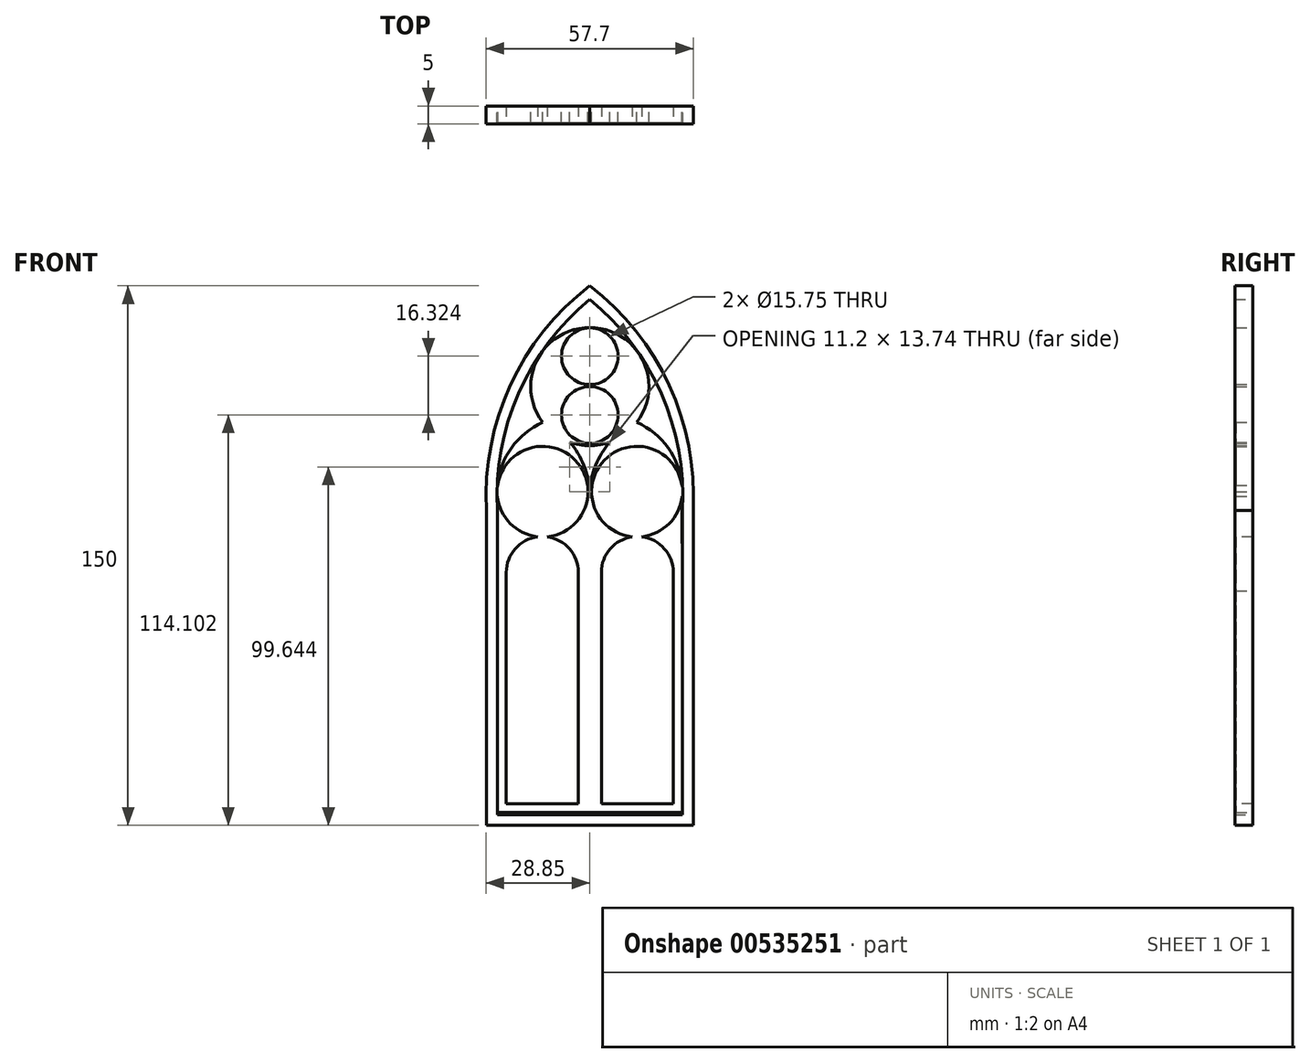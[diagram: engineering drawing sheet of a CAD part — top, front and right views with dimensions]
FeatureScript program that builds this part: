
annotation { "Feature Type Name" : "Feature", "Feature Type Description" : "" }
export const myFeature = defineFeature(function(context is Context, id is Id, definition is map)
    precondition{}
    {
        {
            var Q0;
            Q0=qCreatedBy(makeId("Front.planeOp"),FACE);
            var sketch = newSketch(context, id + "F0", { "sketchPlane" : qUnion([Q0])});
            skLineSegment(sketch, "E0", {"start": v(0, 62.4) * mm, "end": v(0, -107.6) * mm, "construction": true});
            skLineSegment(sketch, "E1", {"start": v(64.93, 0) * mm, "end": v(-64.25, 0) * mm, "construction": true});
            skArc(sketch, "E2", {"start": v(0, 62.4) * mm, "mid": v(-22.1, 34.75) * mm, "end": v(-28.74, 0) * mm});
            skLineSegment(sketch, "E3", {"start": v(-28.74, 0) * mm, "end": v(-28.74, -87.6) * mm});
            skLineSegment(sketch, "E4", {"start": v(-28.74, -87.6) * mm, "end": v(0, -87.6) * mm});
            skArc(sketch, "E5.MirrorCS", {"start": v(0, 62.4) * mm, "mid": v(22.1, 34.75) * mm, "end": v(28.74, 0) * mm});
            skLineSegment(sketch, "E6.MirrorCS", {"start": v(28.74, 0) * mm, "end": v(28.74, -87.6) * mm});
            skLineSegment(sketch, "E7.MirrorCS", {"start": v(28.74, -87.6) * mm, "end": v(0, -87.6) * mm});
            skArc(sketch, "E8.0", {"start": v(0, 58.56) * mm, "mid": v(19.86, 32.4) * mm, "end": v(25.74, 0.08) * mm});
            skLineSegment(sketch, "E8.1", {"start": v(-25.74, 0.08) * mm, "end": v(-25.74, -84.6) * mm});
            skLineSegment(sketch, "E8.2", {"start": v(-25.74, -84.6) * mm, "end": v(-1.32, -84.6) * mm});
            skArc(sketch, "E8.3", {"start": v(0, 58.56) * mm, "mid": v(-19.86, 32.4) * mm, "end": v(-25.74, 0.08) * mm});
            skLineSegment(sketch, "E8.4", {"start": v(25.74, -84.6) * mm, "end": v(-1.32, -84.6) * mm});
            skLineSegment(sketch, "E8.5", {"start": v(25.74, 0.08) * mm, "end": v(25.74, -84.6) * mm});
            skSolve(sketch);
        }
        {
            var Q0;
            Q0=makeQuery(id+"F0.imprint","IMPRINT",FACE,{"disambiguationData":[TD([[makeQuery(id+"F0.imprint","IMPRINT",EDGE,{"derivedFrom":sQuery(id+"F0.wireOp",EDGE,"E2")}),1.0]])]});
            extrude(context, id + "F1", {"entities" : qUnion([Q0]), "depth" : 5 * mm, "offsetDistance" : 25 * mm});
        }
        {
            var Q0;
            Q0=makeQuery(id+"F0.imprint","IMPRINT",FACE,{"disambiguationData":[TD([[makeQuery(id+"F0.imprint","IMPRINT",EDGE,{"derivedFrom":sQuery(id+"F0.wireOp",EDGE,"E8.0")}),-1.0]])]});
            var sketch = newSketch(context, id + "F2", { "sketchPlane" : qUnion([Q0])});
            skLineSegment(sketch, "E9", {"start": v(0, 50.8) * mm, "end": v(0, 50.7) * mm, "construction": true});
            skCircle(sketch, "E10", {"center": v(0, 34.36) * mm, "radius": 16.44 * mm});
            skCircle(sketch, "E11", {"center": v(0, 42.82) * mm, "radius": 7.88 * mm});
            skCircle(sketch, "E12", {"center": v(0, 26.5) * mm, "radius": 7.88 * mm});
            skArc(sketch, "E13", {"start": v(25.65, 6.09) * mm, "mid": v(22, 17.05) * mm, "end": v(13.1, 24.44) * mm});
            skArc(sketch, "E14", {"start": v(13.1, 24.44) * mm, "mid": v(3.84, 16.64) * mm, "end": v(0, 5.16) * mm});
            skLineSegment(sketch, "E15", {"start": v(0, -83.99) * mm, "end": v(25.94, -83.99) * mm});
            skLineSegment(sketch, "E16", {"start": v(25.94, -83.99) * mm, "end": v(25.65, 6.09) * mm});
            skArc(sketch, "E17.MirrorCS", {"start": v(-13.1, 24.44) * mm, "mid": v(-3.84, 16.64) * mm, "end": v(0, 5.16) * mm});
            skArc(sketch, "E18.MirrorCS", {"start": v(-25.65, 6.09) * mm, "mid": v(-22, 17.05) * mm, "end": v(-13.1, 24.44) * mm});
            skLineSegment(sketch, "E19.MirrorCS", {"start": v(-25.94, -83.99) * mm, "end": v(-25.65, 6.09) * mm});
            skLineSegment(sketch, "E20.MirrorCS", {"start": v(0, -83.99) * mm, "end": v(-25.94, -83.99) * mm});
            skPoint(sketch, "E21.orphan", {"position": v(0, 71.38) * mm});
            skLineSegment(sketch, "E22.trimOffspring", {"start": v(0, 34.94) * mm, "end": v(0, 34.36) * mm, "construction": true});
            skLineSegment(sketch, "E23.trimOffspring", {"start": v(0, 18.62) * mm, "end": v(0, 17.92) * mm, "construction": true});
            skLineSegment(sketch, "E24", {"start": v(0, 5.16) * mm, "end": v(0, -83.99) * mm});
            skLineSegment(sketch, "E25", {"start": v(-13.1, 24.44) * mm, "end": v(-13.1, -90.7) * mm, "construction": true});
            skLineSegment(sketch, "E26", {"start": v(13.1, 24.44) * mm, "end": v(13.1, -90.7) * mm, "construction": true});
            skCircle(sketch, "E27", {"center": v(-13.1, 5.16) * mm, "radius": 12.61 * mm});
            skCircle(sketch, "E28", {"center": v(13.1, 5.16) * mm, "radius": 12.61 * mm});
            skSolve(sketch);
        }
        {
            var Q0;
            Q0=makeQuery(id+"F2.imprint","IMPRINT",FACE,{"disambiguationData":[TD([[makeQuery(id+"F2.imprint","IMPRINT",EDGE,{"derivedFrom":sQuery(id+"F2.wireOp",EDGE,"E11")}),-1.0]])]});
            var Q1;
            {var subQ6=sQuery(id+"F2.wireOp",EDGE,"E24");Q1=makeQuery(id+"F2.imprint","IMPRINT",FACE,{"disambiguationData":[TD([[makeQuery(id+"F2.imprint","IMPRINT",EDGE,{"derivedFrom":subQ6}),-1.0]])]});}
            var Q2;
            {var subQ0=sQuery(id+"F2.wireOp",EDGE,"E24");Q2=makeQuery(id+"F2.imprint","IMPRINT",FACE,{"disambiguationData":[TD([[makeQuery(id+"F2.imprint","IMPRINT",EDGE,{"derivedFrom":subQ0}),1.0]])]});}
            var Q3;
            {var subQ0=sQuery(id+"F2.wireOp",EDGE,"E17.MirrorCS");var subQ1=sQuery(id+"F2.wireOp",EDGE,"E10");var subQ3=makeQuery(id+"F2.imprint","INTERSECT",VERTEX,{"derivedFrom":[subQ1,subQ0]});Q3=makeQuery(id+"F2.imprint","IMPRINT",FACE,{"disambiguationData":[TD([[makeQuery(id+"F2.imprint","IMPRINT",EDGE,{"disambiguationData":[TD([[subQ3,1.0]])],"derivedFrom":subQ1}),1.0]])]});}
            var Q4;
            {var subQ0=sQuery(id+"F2.wireOp",EDGE,"E14");var subQ1=sQuery(id+"F2.wireOp",EDGE,"E10");var subQ3=makeQuery(id+"F2.imprint","INTERSECT",VERTEX,{"derivedFrom":[subQ1,subQ0]});Q4=makeQuery(id+"F2.imprint","IMPRINT",FACE,{"disambiguationData":[TD([[makeQuery(id+"F2.imprint","IMPRINT",EDGE,{"disambiguationData":[TD([[subQ3,-1.0]])],"derivedFrom":subQ1}),1.0]])]});}
            extrude(context, id + "F3", {"entities" : qUnion([Q0, Q1, Q2, Q3, Q4]), "operationType" : NewBodyOperationType.ADD, "depth" : 4.7 * mm, "offsetDistance" : 25 * mm});
        }
        {
            var Q0;
            Q0=makeQuery(id+"F3.opExtrude","CAP_FACE",FACE,{"disambiguationData":[OSD([sQuery(id+"F0.wireOp",EDGE,"E8.1"),sQuery(id+"F0.wireOp",EDGE,"E8.5"),sQuery(id+"F2.wireOp",EDGE,"E10"),sQuery(id+"F2.wireOp",EDGE,"E11"),sQuery(id+"F2.wireOp",EDGE,"E12"),sQuery(id+"F2.wireOp",EDGE,"E13"),sQuery(id+"F2.wireOp",EDGE,"E14"),sQuery(id+"F2.wireOp",EDGE,"E15"),sQuery(id+"F2.wireOp",EDGE,"E16"),sQuery(id+"F2.wireOp",EDGE,"E17.MirrorCS"),sQuery(id+"F2.wireOp",EDGE,"E18.MirrorCS"),sQuery(id+"F2.wireOp",EDGE,"E19.MirrorCS"),sQuery(id+"F2.wireOp",EDGE,"E20.MirrorCS"),sQuery(id+"F2.wireOp",EDGE,"E27"),sQuery(id+"F2.wireOp",EDGE,"E28")])],"isStart":false});
            var sketch = newSketch(context, id + "F4", { "sketchPlane" : qUnion([Q0])});
            skLineSegment(sketch, "E29.bottom", {"start": v(-13.2, -7.3) * mm, "end": v(-13.2, -7.3) * mm});
            skLineSegment(sketch, "E29.top", {"start": v(-23.2, -81.61) * mm, "end": v(-3.2, -81.61) * mm});
            skLineSegment(sketch, "E29.left", {"start": v(-23.2, -17.3) * mm, "end": v(-23.2, -81.61) * mm});
            skLineSegment(sketch, "E29.right", {"start": v(-3.2, -17.3) * mm, "end": v(-3.2, -81.61) * mm});
            skLineSegment(sketch, "E30.MirrorCS", {"start": v(13.2, -7.3) * mm, "end": v(13.2, -7.3) * mm});
            skLineSegment(sketch, "E31.MirrorCS", {"start": v(3.2, -17.3) * mm, "end": v(3.2, -81.61) * mm});
            skLineSegment(sketch, "E32.MirrorCS", {"start": v(23.2, -17.3) * mm, "end": v(23.2, -81.61) * mm});
            skLineSegment(sketch, "E33.MirrorCS", {"start": v(23.2, -81.61) * mm, "end": v(3.2, -81.61) * mm});
            skPoint(sketch, "E34.visualSharp", {"position": v(-23.2, -7.3) * mm});
            skArc(sketch, "E34.filletArc", {"start": v(-13.2, -7.3) * mm, "mid": v(-20.28, -10.22) * mm, "end": v(-23.2, -17.3) * mm});
            skPoint(sketch, "E35.visualSharp", {"position": v(-3.2, -7.3) * mm});
            skArc(sketch, "E35.filletArc", {"start": v(-3.2, -17.3) * mm, "mid": v(-6.14, -10.22) * mm, "end": v(-13.2, -7.3) * mm});
            skPoint(sketch, "E36.visualSharp", {"position": v(3.2, -7.3) * mm});
            skArc(sketch, "E36.filletArc", {"start": v(13.2, -7.3) * mm, "mid": v(6.14, -10.22) * mm, "end": v(3.2, -17.3) * mm});
            skPoint(sketch, "E37.visualSharp", {"position": v(23.2, -7.3) * mm});
            skArc(sketch, "E37.filletArc", {"start": v(23.2, -17.3) * mm, "mid": v(20.28, -10.22) * mm, "end": v(13.2, -7.3) * mm});
            skSolve(sketch);
        }
        {
            var Q0;
            Q0=makeQuery(id+"F4.imprint","IMPRINT",FACE,{"disambiguationData":[TD([[makeQuery(id+"F4.imprint","IMPRINT",EDGE,{"derivedFrom":sQuery(id+"F4.wireOp",EDGE,"E29.top")}),1.0]])]});
            var Q1;
            {var subQ1=sQuery(id+"F4.wireOp",EDGE,"E31.MirrorCS");Q1=makeQuery(id+"F4.imprint","IMPRINT",FACE,{"disambiguationData":[TD([[makeQuery(id+"F4.imprint","IMPRINT",EDGE,{"derivedFrom":subQ1}),1.0]])]});}
            extrude(context, id + "F5", {"entities" : qUnion([Q0, Q1]), "operationType" : NewBodyOperationType.REMOVE, "endBound" : BoundingType.UP_TO_NEXT, "oppositeDirection" : true, "depth" : 25 * mm, "offsetDistance" : 25 * mm});
        }
    });
